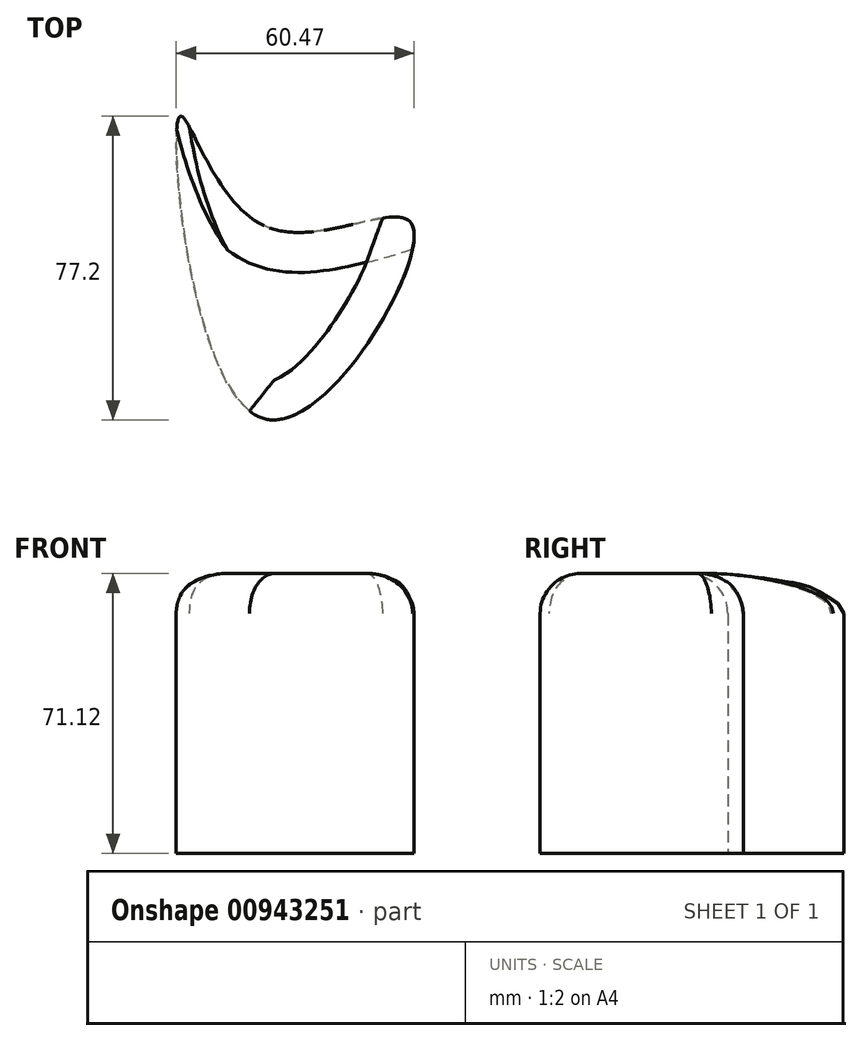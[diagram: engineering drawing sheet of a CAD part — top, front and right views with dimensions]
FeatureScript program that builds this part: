
annotation { "Feature Type Name" : "Feature", "Feature Type Description" : "" }
export const myFeature = defineFeature(function(context is Context, id is Id, definition is map)
    precondition{}
    {
        {
            var Q0;
            Q0=qCreatedBy(makeId("Top.planeOp"),FACE);
            var sketch = newSketch(context, id + "F0", { "sketchPlane" : qUnion([Q0])});
            skFitSpline(sketch, "E0", {"points": [v(0, 0) * mm, v(-21.57, 27.6) * mm, v(0, -49.04) * mm, v(37.72, 0) * mm, v(0, 0) * mm]});
            skSolve(sketch);
        }
        {
            var Q0;
            Q0 = qSketchRegion(id + "F0", true);
            extrude(context, id + "F1", {"entities" : qUnion([Q0]), "depth" : 71.12 * mm, "offsetDistance" : 25.4 * mm});
        }
        {
            var Q0;
            Q0=makeQuery(id+"F1.opExtrude","CAP_EDGE",EDGE,{"disambiguationData":[OSD([sQuery(id+"F0.wireOp",EDGE,"E0")])],"isStart":false});
            fillet(context, id + "F2", {"entities" : qUnion([Q0]), "radius" : 10.16 * mm, "tangentPropagation" : true, "allowEdgeOverflow" : false});
        }
    });
